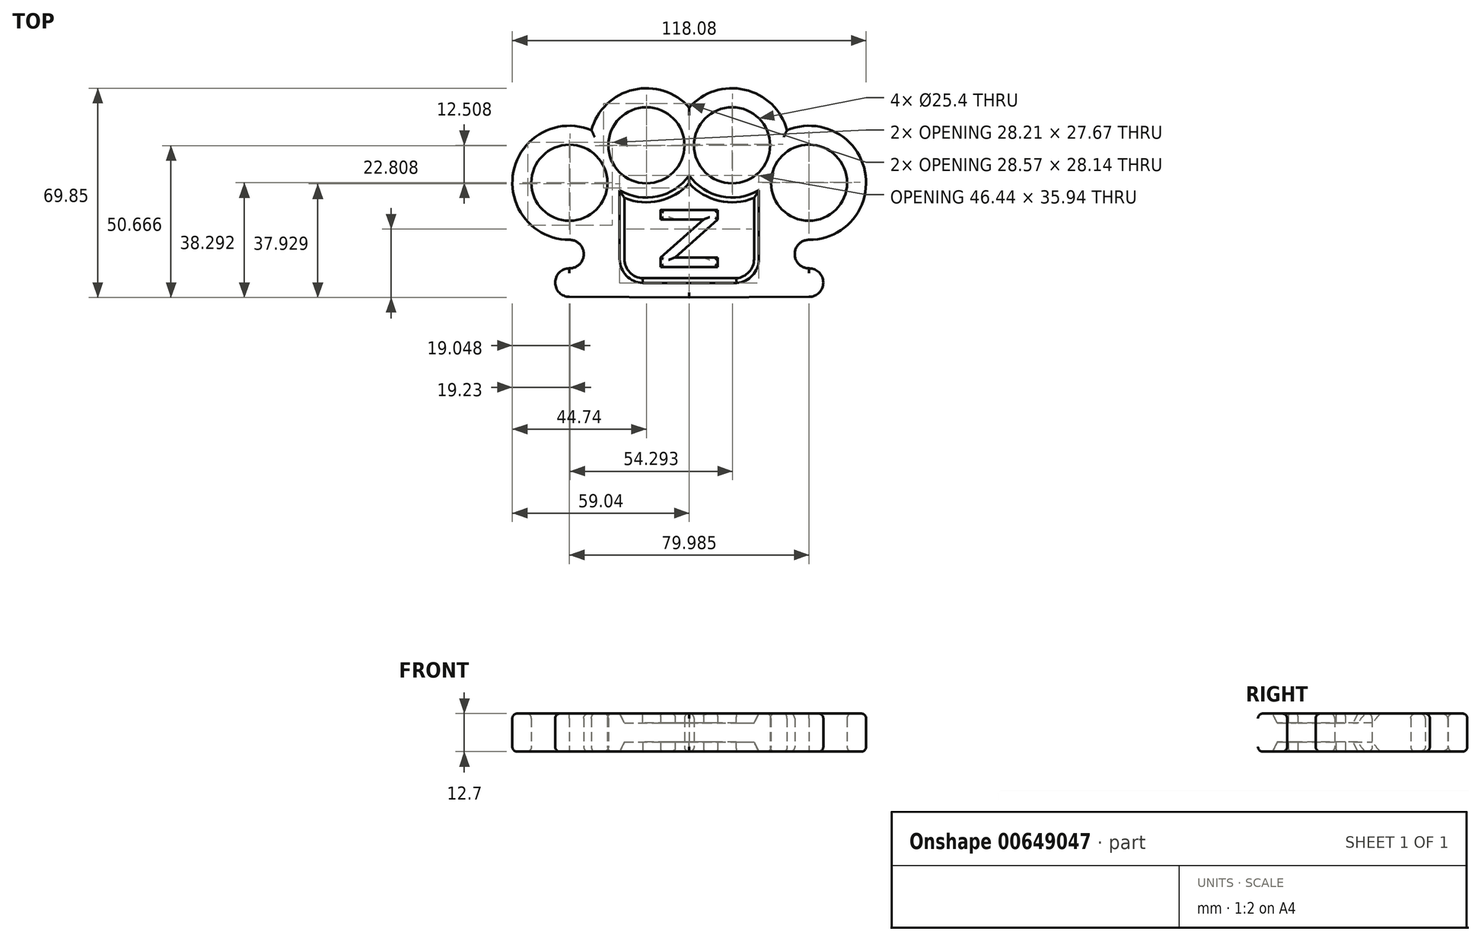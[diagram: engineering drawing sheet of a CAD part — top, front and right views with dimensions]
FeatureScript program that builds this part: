
annotation { "Feature Type Name" : "Feature", "Feature Type Description" : "" }
export const myFeature = defineFeature(function(context is Context, id is Id, definition is map)
    precondition{}
    {
        {
            var Q0;
            Q0=qCreatedBy(makeId("Top.planeOp"),FACE);
            var sketch = newSketch(context, id + "F0", { "sketchPlane" : qUnion([Q0])});
            skCircle(sketch, "E0", {"center": v(14.3, 25.4) * mm, "radius": 12.7 * mm});
            skCircle(sketch, "E1", {"center": v(40, 12.9) * mm, "radius": 12.7 * mm});
            skArc(sketch, "E2", {"start": v(40, -6.16) * mm, "mid": v(58.67, 16.63) * mm, "end": v(32.66, 30.48) * mm});
            skArc(sketch, "E3", {"start": v(32.66, 30.48) * mm, "mid": v(18.57, 43.97) * mm, "end": v(0, 37.99) * mm});
            skPoint(sketch, "E4", {"position": v(40, -25.2) * mm});
            skArc(sketch, "E5", {"start": v(40, -6.16) * mm, "mid": v(35.21, -10.93) * mm, "end": v(40, -15.68) * mm});
            skLineSegment(sketch, "E6", {"start": v(40, -25.2) * mm, "end": v(0, -25.4) * mm});
            skLineSegment(sketch, "E7", {"start": v(58.76, 9.64) * mm, "end": v(58.67, 9.15) * mm});
            skPoint(sketch, "E7.endSnap0", {"position": v(58.67, 16.63) * mm});
            skLineSegment(sketch, "E8", {"start": v(0, 75.74) * mm, "end": v(0, -56.8) * mm});
            skLineSegment(sketch, "E9.MirrorCS", {"start": v(-40, -25.2) * mm, "end": v(0, -25.4) * mm});
            skArc(sketch, "E10.MirrorCS", {"start": v(-40, -25.2) * mm, "mid": v(-44.74, -20.45) * mm, "end": v(-40, -15.68) * mm});
            skArc(sketch, "E11.MirrorCS", {"start": v(-40, -6.16) * mm, "mid": v(-35.21, -10.93) * mm, "end": v(-40, -15.68) * mm});
            skArc(sketch, "E12.MirrorCS", {"start": v(-40, -6.16) * mm, "mid": v(-58.67, 16.63) * mm, "end": v(-32.66, 30.48) * mm});
            skCircle(sketch, "E13.MirrorC", {"center": v(-40, 12.9) * mm, "radius": 12.7 * mm});
            skCircle(sketch, "E14.MirrorC", {"center": v(-14.3, 25.4) * mm, "radius": 12.7 * mm});
            skArc(sketch, "E15.MirrorCS", {"start": v(-32.66, 30.48) * mm, "mid": v(-18.57, 43.97) * mm, "end": v(0, 37.99) * mm});
            skArc(sketch, "E16.MirrorCS", {"start": v(40, -25.2) * mm, "mid": v(44.74, -20.45) * mm, "end": v(40, -15.68) * mm});
            skLineSegment(sketch, "E17.MirrorCS", {"start": v(-58.76, 9.64) * mm, "end": v(-58.67, 9.15) * mm});
            skPoint(sketch, "E18.orphan", {"position": v(-25.9, 54.96) * mm});
            skPoint(sketch, "E19.MirrorCS.end.orphan", {"position": v(-32.66, 30.48) * mm});
            skPoint(sketch, "E20.MirrorCS.start.orphan", {"position": v(0, 37.99) * mm});
            skPoint(sketch, "E21.start.orphan", {"position": v(25.9, 54.96) * mm});
            skPoint(sketch, "E22.orphan", {"position": v(65.18, 44.03) * mm});
            skPoint(sketch, "E23.MirrorCS.end.orphan", {"position": v(-65.18, 44.03) * mm});
            skArc(sketch, "E24", {"start": v(-21.63, 7.82) * mm, "mid": v(-10.01, 6.84) * mm, "end": v(0, 12.81) * mm});
            skArc(sketch, "E25", {"start": v(0, 12.81) * mm, "mid": v(10.01, 6.84) * mm, "end": v(21.63, 7.82) * mm});
            skLineSegment(sketch, "E26", {"start": v(-21.63, 7.82) * mm, "end": v(-21.63, -12.6) * mm});
            skLineSegment(sketch, "E27", {"start": v(21.63, 7.82) * mm, "end": v(21.63, -12.6) * mm});
            skArc(sketch, "E28", {"start": v(-21.63, -12.6) * mm, "mid": v(-19.85, -17.04) * mm, "end": v(-15.47, -18.97) * mm});
            skArc(sketch, "E29", {"start": v(21.63, -12.6) * mm, "mid": v(19.94, -16.94) * mm, "end": v(15.74, -18.96) * mm});
            skLineSegment(sketch, "E30", {"start": v(15.74, -18.96) * mm, "end": v(-15.47, -18.97) * mm});
            skPoint(sketch, "E31", {"position": v(-59.04, 12.9) * mm});
            skPoint(sketch, "E32", {"position": v(59.04, 12.9) * mm});
            skPoint(sketch, "E33", {"position": v(14.3, 44.45) * mm});
            skSolve(sketch);
        }
        {
            var Q0;
            Q0 = qSketchRegion(id + "F0", true);
            extrude(context, id + "F1", {"entities" : qUnion([Q0]), "depth" : 12.7 * mm, "offsetDistance" : 25.4 * mm});
        }
        {
            var Q0;
            {var subQ1=sQuery(id+"F0.wireOp",EDGE,"E24");Q0=makeQuery(id+"F0.imprint","IMPRINT",FACE,{"disambiguationData":[TD([[makeQuery(id+"F0.imprint","IMPRINT",EDGE,{"derivedFrom":subQ1}),-1.0]])]});}
            var Q1;
            {var subQ1=sQuery(id+"F0.wireOp",EDGE,"E25");Q1=makeQuery(id+"F0.imprint","IMPRINT",FACE,{"disambiguationData":[TD([[makeQuery(id+"F0.imprint","IMPRINT",EDGE,{"derivedFrom":subQ1}),-1.0]])]});}
            extrude(context, id + "F2", {"entities" : qUnion([Q0, Q1]), "operationType" : NewBodyOperationType.ADD, "depth" : 9.52 * mm, "offsetDistance" : 25.4 * mm, "hasSecondDirection" : true, "secondDirectionOppositeDirection" : false, "secondDirectionDepth" : 3.17 * mm});
        }
        {
            var Q0;
            Q0=qCreatedBy(makeId("Top.planeOp"),FACE);
            var sketch = newSketch(context, id + "F3", { "sketchPlane" : qUnion([Q0])});
            skLineSegment(sketch, "E34.bottom", {"start": v(-9.53, 3.82) * mm, "end": v(9.53, 3.82) * mm, "construction": true});
            skLineSegment(sketch, "E34.top", {"start": v(-9.53, -15.23) * mm, "end": v(9.53, -15.23) * mm, "construction": true});
            skLineSegment(sketch, "E34.left", {"start": v(-9.53, 3.82) * mm, "end": v(-9.53, -15.23) * mm, "construction": true});
            skLineSegment(sketch, "E34.right", {"start": v(9.53, 3.82) * mm, "end": v(9.53, -15.23) * mm, "construction": true});
            skLineSegment(sketch, "E35", {"start": v(-9.53, 3.82) * mm, "end": v(9.53, 3.82) * mm});
            skLineSegment(sketch, "E36", {"start": v(-9.53, -15.23) * mm, "end": v(9.53, -15.23) * mm});
            skLineSegment(sketch, "E37", {"start": v(9.53, -15.23) * mm, "end": v(9.53, -12.05) * mm});
            skLineSegment(sketch, "E38", {"start": v(9.53, -12.05) * mm, "end": v(-4.76, -12.05) * mm});
            skLineSegment(sketch, "E39", {"start": v(-4.76, -12.05) * mm, "end": v(9.53, 0.65) * mm});
            skLineSegment(sketch, "E40", {"start": v(9.53, 0.65) * mm, "end": v(9.53, 3.82) * mm});
            skLineSegment(sketch, "E41", {"start": v(-9.53, 3.82) * mm, "end": v(-9.53, 0.65) * mm});
            skLineSegment(sketch, "E42", {"start": v(-9.52, 0.65) * mm, "end": v(4.76, 0.65) * mm});
            skLineSegment(sketch, "E43", {"start": v(4.76, 0.65) * mm, "end": v(-9.53, -12.05) * mm});
            skLineSegment(sketch, "E44", {"start": v(-9.52, -12.05) * mm, "end": v(-9.52, -15.23) * mm});
            skSolve(sketch);
        }
        {
            var Q0;
            Q0 = qSketchRegion(id + "F3", true);
            extrude(context, id + "F4", {"entities" : qUnion([Q0]), "operationType" : NewBodyOperationType.ADD, "depth" : 12.7 * mm, "offsetDistance" : 25.4 * mm, "hasSecondDirection" : true, "secondDirectionOppositeDirection" : false, "secondDirectionDepth" : 6.35 * mm});
        }
        {
            var Q0;
            Q0=makeQuery(id+"F0.imprint","IMPRINT",FACE,{"disambiguationData":[TD([[makeQuery(id+"F0.imprint","IMPRINT",EDGE,{"derivedFrom":sQuery(id+"F0.wireOp",EDGE,"E0")}),1.0]])]});
            var sketch = newSketch(context, id + "F5", { "sketchPlane" : qUnion([Q0])});
            skLineSegment(sketch, "E45", {"start": v(9.46, 3.82) * mm, "end": v(-9.55, 3.82) * mm});
            skLineSegment(sketch, "E46", {"start": v(-9.55, 3.82) * mm, "end": v(-9.52, 0.65) * mm});
            skLineSegment(sketch, "E47", {"start": v(-9.52, 0.65) * mm, "end": v(4.76, -12.05) * mm});
            skLineSegment(sketch, "E48", {"start": v(4.76, -12.05) * mm, "end": v(-9.53, -12.05) * mm});
            skLineSegment(sketch, "E49", {"start": v(-9.53, -12.05) * mm, "end": v(-9.6, -15.23) * mm});
            skLineSegment(sketch, "E50", {"start": v(-9.6, -15.23) * mm, "end": v(9.53, -15.23) * mm});
            skLineSegment(sketch, "E51", {"start": v(9.53, -15.23) * mm, "end": v(9.53, -12.05) * mm});
            skLineSegment(sketch, "E52", {"start": v(9.53, -12.05) * mm, "end": v(-4.76, 0.65) * mm});
            skLineSegment(sketch, "E53", {"start": v(-4.76, 0.65) * mm, "end": v(9.52, 0.65) * mm});
            skLineSegment(sketch, "E54", {"start": v(9.53, 0.65) * mm, "end": v(9.46, 3.82) * mm});
            skSolve(sketch);
        }
        {
            var Q0;
            Q0 = qSketchRegion(id + "F5", true);
            extrude(context, id + "F6", {"entities" : qUnion([Q0]), "operationType" : NewBodyOperationType.ADD, "depth" : 6.35 * mm, "offsetDistance" : 25.4 * mm});
        }
        {
            var Q0;
            Q0=makeQuery(id+"F1.opExtrude","CAP_EDGE",EDGE,{"disambiguationData":[OSD([sQuery(id+"F0.wireOp",EDGE,"E6")])],"isStart":false});
            var Q1;
            Q1=makeQuery(id+"F1.opExtrude","CAP_EDGE",EDGE,{"disambiguationData":[OSD([sQuery(id+"F0.wireOp",EDGE,"E9.MirrorCS")])],"isStart":false});
            var Q2;
            Q2=makeQuery(id+"F1.opExtrude","CAP_EDGE",EDGE,{"disambiguationData":[OSD([sQuery(id+"F0.wireOp",EDGE,"E16.MirrorCS")])],"isStart":false});
            var Q3;
            Q3=makeQuery(id+"F1.opExtrude","CAP_EDGE",EDGE,{"disambiguationData":[OSD([sQuery(id+"F0.wireOp",EDGE,"E5")])],"isStart":false});
            var Q4;
            Q4=makeQuery(id+"F1.opExtrude","CAP_EDGE",EDGE,{"disambiguationData":[OSD([sQuery(id+"F0.wireOp",EDGE,"E2")])],"isStart":false});
            var Q5;
            Q5=makeQuery(id+"F1.opExtrude","CAP_EDGE",EDGE,{"disambiguationData":[OSD([sQuery(id+"F0.wireOp",EDGE,"E3")])],"isStart":false});
            var Q6;
            Q6=makeQuery(id+"F1.opExtrude","CAP_EDGE",EDGE,{"disambiguationData":[OSD([sQuery(id+"F0.wireOp",EDGE,"E15.MirrorCS")])],"isStart":false});
            var Q7;
            Q7=makeQuery(id+"F1.opExtrude","CAP_EDGE",EDGE,{"disambiguationData":[OSD([sQuery(id+"F0.wireOp",EDGE,"E12.MirrorCS")])],"isStart":false});
            var Q8;
            Q8=makeQuery(id+"F1.opExtrude","CAP_EDGE",EDGE,{"disambiguationData":[OSD([sQuery(id+"F0.wireOp",EDGE,"E11.MirrorCS")])],"isStart":false});
            var Q9;
            Q9=makeQuery(id+"F1.opExtrude","CAP_EDGE",EDGE,{"disambiguationData":[OSD([sQuery(id+"F0.wireOp",EDGE,"E10.MirrorCS")])],"isStart":false});
            var Q10;
            Q10=makeQuery(id+"F1.opExtrude","CAP_EDGE",EDGE,{"disambiguationData":[OSD([sQuery(id+"F0.wireOp",EDGE,"E1")])],"isStart":false});
            var Q11;
            Q11=makeQuery(id+"F1.opExtrude","CAP_EDGE",EDGE,{"disambiguationData":[OSD([sQuery(id+"F0.wireOp",EDGE,"E0")])],"isStart":false});
            var Q12;
            Q12=makeQuery(id+"F1.opExtrude","CAP_EDGE",EDGE,{"disambiguationData":[OSD([sQuery(id+"F0.wireOp",EDGE,"E14.MirrorC")])],"isStart":false});
            var Q13;
            Q13=makeQuery(id+"F1.opExtrude","CAP_EDGE",EDGE,{"disambiguationData":[OSD([sQuery(id+"F0.wireOp",EDGE,"E13.MirrorC")])],"isStart":false});
            var Q14;
            Q14=makeQuery(id+"F1.opExtrude","CAP_EDGE",EDGE,{"disambiguationData":[OSD([sQuery(id+"F0.wireOp",EDGE,"E14.MirrorC")])],"isStart":true});
            var Q15;
            Q15=makeQuery(id+"F1.opExtrude","CAP_EDGE",EDGE,{"disambiguationData":[OSD([sQuery(id+"F0.wireOp",EDGE,"E15.MirrorCS")])],"isStart":true});
            var Q16;
            Q16=makeQuery(id+"F1.opExtrude","CAP_EDGE",EDGE,{"disambiguationData":[OSD([sQuery(id+"F0.wireOp",EDGE,"E0")])],"isStart":true});
            var Q17;
            Q17=makeQuery(id+"F1.opExtrude","CAP_EDGE",EDGE,{"disambiguationData":[OSD([sQuery(id+"F0.wireOp",EDGE,"E3")])],"isStart":true});
            var Q18;
            Q18=makeQuery(id+"F1.opExtrude","CAP_EDGE",EDGE,{"disambiguationData":[OSD([sQuery(id+"F0.wireOp",EDGE,"E13.MirrorC")])],"isStart":true});
            var Q19;
            Q19=makeQuery(id+"F1.opExtrude","CAP_EDGE",EDGE,{"disambiguationData":[OSD([sQuery(id+"F0.wireOp",EDGE,"E12.MirrorCS")])],"isStart":true});
            var Q20;
            Q20=makeQuery(id+"F1.opExtrude","CAP_EDGE",EDGE,{"disambiguationData":[OSD([sQuery(id+"F0.wireOp",EDGE,"E10.MirrorCS")])],"isStart":true});
            var Q21;
            Q21=makeQuery(id+"F1.opExtrude","CAP_EDGE",EDGE,{"disambiguationData":[OSD([sQuery(id+"F0.wireOp",EDGE,"E9.MirrorCS")])],"isStart":true});
            var Q22;
            Q22=makeQuery(id+"F1.opExtrude","CAP_EDGE",EDGE,{"disambiguationData":[OSD([sQuery(id+"F0.wireOp",EDGE,"E11.MirrorCS")])],"isStart":true});
            var Q23;
            Q23=makeQuery(id+"F1.opExtrude","CAP_EDGE",EDGE,{"disambiguationData":[OSD([sQuery(id+"F0.wireOp",EDGE,"E2")])],"isStart":true});
            var Q24;
            Q24=makeQuery(id+"F1.opExtrude","CAP_EDGE",EDGE,{"disambiguationData":[OSD([sQuery(id+"F0.wireOp",EDGE,"E1")])],"isStart":true});
            var Q25;
            Q25=makeQuery(id+"F1.opExtrude","CAP_EDGE",EDGE,{"disambiguationData":[OSD([sQuery(id+"F0.wireOp",EDGE,"E16.MirrorCS")])],"isStart":true});
            var Q26;
            Q26=makeQuery(id+"F1.opExtrude","CAP_EDGE",EDGE,{"disambiguationData":[OSD([sQuery(id+"F0.wireOp",EDGE,"E6")])],"isStart":true});
            var Q27;
            Q27=makeQuery(id+"F1.opExtrude","CAP_EDGE",EDGE,{"disambiguationData":[OSD([sQuery(id+"F0.wireOp",EDGE,"E5")])],"isStart":true});
            fillet(context, id + "F7", {"entities" : qUnion([Q0, Q1, Q2, Q3, Q4, Q5, Q6, Q7, Q8, Q9, Q10, Q11, Q12, Q13, Q14, Q15, Q16, Q17, Q18, Q19, Q20, Q21, Q22, Q23, Q24, Q25, Q26, Q27]), "radius" : 1.59 * mm, "tangentPropagation" : true, "allowEdgeOverflow" : false});
        }
        {
            var Q0;
            Q0=makeQuery(id+"F1.opExtrude","CAP_EDGE",EDGE,{"disambiguationData":[OSD([sQuery(id+"F0.wireOp",EDGE,"E27")])],"isStart":false});
            var Q1;
            Q1=makeQuery(id+"F1.opExtrude","CAP_EDGE",EDGE,{"disambiguationData":[OSD([sQuery(id+"F0.wireOp",EDGE,"E29")])],"isStart":false});
            var Q2;
            Q2=makeQuery(id+"F1.opExtrude","CAP_EDGE",EDGE,{"disambiguationData":[OSD([sQuery(id+"F0.wireOp",EDGE,"E30")])],"isStart":false});
            var Q3;
            Q3=makeQuery(id+"F1.opExtrude","CAP_EDGE",EDGE,{"disambiguationData":[OSD([sQuery(id+"F0.wireOp",EDGE,"E25")])],"isStart":false});
            var Q4;
            Q4=makeQuery(id+"F1.opExtrude","CAP_EDGE",EDGE,{"disambiguationData":[OSD([sQuery(id+"F0.wireOp",EDGE,"E24")])],"isStart":false});
            var Q5;
            Q5=makeQuery(id+"F1.opExtrude","CAP_EDGE",EDGE,{"disambiguationData":[OSD([sQuery(id+"F0.wireOp",EDGE,"E26")])],"isStart":false});
            var Q6;
            Q6=makeQuery(id+"F1.opExtrude","CAP_EDGE",EDGE,{"disambiguationData":[OSD([sQuery(id+"F0.wireOp",EDGE,"E28")])],"isStart":false});
            chamfer(context, id + "F8", {"entities" : qUnion([Q0, Q1, Q2, Q3, Q4, Q5, Q6]), "chamferType" : ChamferType.TWO_OFFSETS, "width1" : 1.59 * mm, "oppositeDirection" : false, "width2" : 3.17 * mm, "tangentPropagation" : true});
        }
        {
            var Q0;
            Q0=makeQuery(id+"F1.opExtrude","CAP_EDGE",EDGE,{"disambiguationData":[OSD([sQuery(id+"F0.wireOp",EDGE,"E24")])],"isStart":true});
            var Q1;
            Q1=makeQuery(id+"F1.opExtrude","CAP_EDGE",EDGE,{"disambiguationData":[OSD([sQuery(id+"F0.wireOp",EDGE,"E25")])],"isStart":true});
            var Q2;
            Q2=makeQuery(id+"F1.opExtrude","CAP_EDGE",EDGE,{"disambiguationData":[OSD([sQuery(id+"F0.wireOp",EDGE,"E26")])],"isStart":true});
            var Q3;
            Q3=makeQuery(id+"F1.opExtrude","CAP_EDGE",EDGE,{"disambiguationData":[OSD([sQuery(id+"F0.wireOp",EDGE,"E28")])],"isStart":true});
            var Q4;
            Q4=makeQuery(id+"F1.opExtrude","CAP_EDGE",EDGE,{"disambiguationData":[OSD([sQuery(id+"F0.wireOp",EDGE,"E29")])],"isStart":true});
            var Q5;
            Q5=makeQuery(id+"F1.opExtrude","CAP_EDGE",EDGE,{"disambiguationData":[OSD([sQuery(id+"F0.wireOp",EDGE,"E27")])],"isStart":true});
            var Q6;
            Q6=makeQuery(id+"F1.opExtrude","CAP_EDGE",EDGE,{"disambiguationData":[OSD([sQuery(id+"F0.wireOp",EDGE,"E30")])],"isStart":true});
            chamfer(context, id + "F9", {"entities" : qUnion([Q0, Q1, Q2, Q3, Q4, Q5, Q6]), "chamferType" : ChamferType.TWO_OFFSETS, "width1" : 3.17 * mm, "oppositeDirection" : false, "width2" : 1.59 * mm, "tangentPropagation" : true});
        }
        {
            var Q0;
            Q0=makeQuery(id+"F4.opExtrude","CAP_FACE",FACE,{"disambiguationData":[OSD([sQuery(id+"F3.wireOp",EDGE,"E35"),sQuery(id+"F3.wireOp",EDGE,"E36"),sQuery(id+"F3.wireOp",EDGE,"E37"),sQuery(id+"F3.wireOp",EDGE,"E38"),sQuery(id+"F3.wireOp",EDGE,"E39"),sQuery(id+"F3.wireOp",EDGE,"E40"),sQuery(id+"F3.wireOp",EDGE,"E41"),sQuery(id+"F3.wireOp",EDGE,"E42"),sQuery(id+"F3.wireOp",EDGE,"E43"),sQuery(id+"F3.wireOp",EDGE,"E44")])],"isStart":false});
            var Q1;
            Q1=makeQuery(id+"F6.opExtrude","CAP_FACE",FACE,{"disambiguationData":[OSD([sQuery(id+"F5.wireOp",EDGE,"E45"),sQuery(id+"F5.wireOp",EDGE,"E46"),sQuery(id+"F5.wireOp",EDGE,"E47"),sQuery(id+"F5.wireOp",EDGE,"E48"),sQuery(id+"F5.wireOp",EDGE,"E49"),sQuery(id+"F5.wireOp",EDGE,"E50"),sQuery(id+"F5.wireOp",EDGE,"E51"),sQuery(id+"F5.wireOp",EDGE,"E52"),sQuery(id+"F5.wireOp",EDGE,"E53"),sQuery(id+"F5.wireOp",EDGE,"E54")])],"isStart":true});
            fillet(context, id + "F10", {"entities" : qUnion([Q0, Q1]), "radius" : 0.8 * mm, "tangentPropagation" : true, "allowEdgeOverflow" : false});
        }
    });
